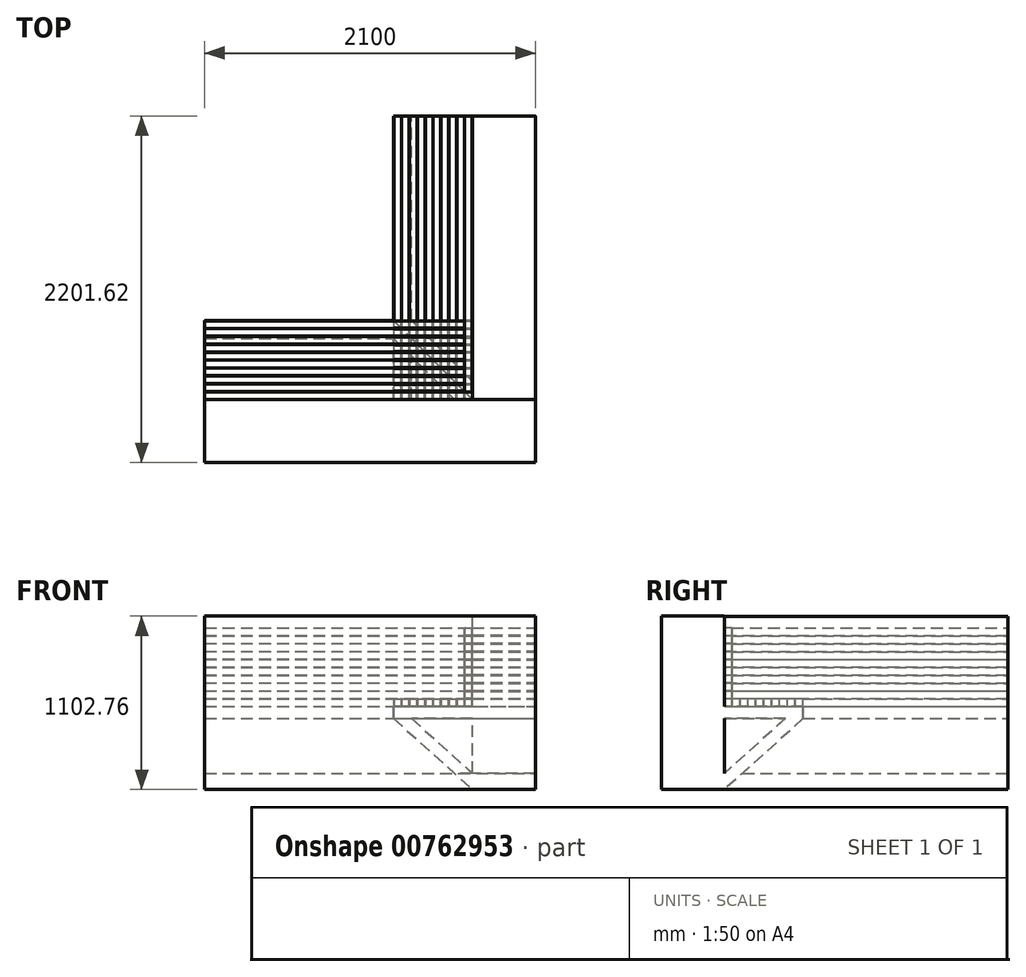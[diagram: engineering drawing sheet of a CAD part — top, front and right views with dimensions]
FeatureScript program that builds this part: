
annotation { "Feature Type Name" : "Feature", "Feature Type Description" : "" }
export const myFeature = defineFeature(function(context is Context, id is Id, definition is map)
    precondition{}
    {
        {
            var Q0;
            Q0=qCreatedBy(makeId("Front.planeOp"),FACE);
            var sketch = newSketch(context, id + "F0", { "sketchPlane" : qUnion([Q0])});
            skLineSegment(sketch, "E0", {"start": v(1, 650) * mm, "end": v(399, 650) * mm});
            skLineSegment(sketch, "E1", {"start": v(400, 649) * mm, "end": v(400, -449) * mm});
            skLineSegment(sketch, "E2", {"start": v(399, -450) * mm, "end": v(0, -450) * mm});
            skLineSegment(sketch, "E3", {"start": v(0, -450) * mm, "end": v(0, 0) * mm});
            skLineSegment(sketch, "E4", {"start": v(0, 0) * mm, "end": v(-500, 0) * mm});
            skLineSegment(sketch, "E5", {"start": v(-500, 0) * mm, "end": v(-500, 75.2) * mm});
            skLineSegment(sketch, "E6", {"start": v(-499, 76.2) * mm, "end": v(0, 76.2) * mm});
            skLineSegment(sketch, "E7", {"start": v(0, 76.2) * mm, "end": v(0, 649) * mm});
            skLineSegment(sketch, "E8", {"start": v(-500, 0) * mm, "end": v(0, -450) * mm});
            skLineSegment(sketch, "E9", {"start": v(-386.1, 0) * mm, "end": v(0, -347.48) * mm});
            skPoint(sketch, "E10.visualSharp", {"position": v(-500, 76.2) * mm});
            skArc(sketch, "E10.filletArc", {"start": v(-499, 76.2) * mm, "mid": v(-499.7, 75.9) * mm, "end": v(-500, 75.2) * mm});
            skPoint(sketch, "E11.visualSharp", {"position": v(0, 650) * mm});
            skArc(sketch, "E11.filletArc", {"start": v(1, 650) * mm, "mid": v(0.3, 649.7) * mm, "end": v(0, 649) * mm});
            skPoint(sketch, "E12.visualSharp", {"position": v(400, 650) * mm});
            skArc(sketch, "E12.filletArc", {"start": v(400, 649) * mm, "mid": v(399.7, 649.7) * mm, "end": v(399, 650) * mm});
            skPoint(sketch, "E13.visualSharp", {"position": v(400, -450) * mm});
            skArc(sketch, "E13.filletArc", {"start": v(399, -450) * mm, "mid": v(399.7, -449.7) * mm, "end": v(400, -449) * mm});
            skLineSegment(sketch, "E14.bottom", {"start": v(-4.84, 124.92) * mm, "end": v(-44.84, 124.92) * mm});
            skLineSegment(sketch, "E14.top", {"start": v(-4.84, 76.92) * mm, "end": v(-44.84, 76.92) * mm});
            skLineSegment(sketch, "E14.left", {"start": v(-0.84, 120.92) * mm, "end": v(-0.84, 80.92) * mm});
            skLineSegment(sketch, "E14.right", {"start": v(-48.84, 120.92) * mm, "end": v(-48.84, 80.92) * mm});
            skPoint(sketch, "E15.visualSharp", {"position": v(-48.84, 124.92) * mm});
            skArc(sketch, "E15.filletArc", {"start": v(-44.84, 124.92) * mm, "mid": v(-47.66, 123.75) * mm, "end": v(-48.84, 120.92) * mm});
            skPoint(sketch, "E16.visualSharp", {"position": v(-0.84, 124.92) * mm});
            skArc(sketch, "E16.filletArc", {"start": v(-0.84, 120.92) * mm, "mid": v(-2, 123.75) * mm, "end": v(-4.84, 124.92) * mm});
            skPoint(sketch, "E17.visualSharp", {"position": v(-48.84, 76.92) * mm});
            skArc(sketch, "E17.filletArc", {"start": v(-48.84, 80.92) * mm, "mid": v(-47.66, 78.1) * mm, "end": v(-44.84, 76.92) * mm});
            skPoint(sketch, "E18.visualSharp", {"position": v(-0.84, 76.92) * mm});
            skArc(sketch, "E18.filletArc", {"start": v(-4.84, 76.92) * mm, "mid": v(-2, 78.1) * mm, "end": v(-0.84, 80.92) * mm});
            skLineSegment(sketch, "E19.1.0.0", {"start": v(-50.84, 120.92) * mm, "end": v(-50.84, 80.92) * mm});
            skPoint(sketch, "E19.1.0.1", {"position": v(-50.84, 124.92) * mm});
            skArc(sketch, "E19.1.0.2", {"start": v(-50.84, 120.92) * mm, "mid": v(-52, 123.75) * mm, "end": v(-54.84, 124.92) * mm});
            skLineSegment(sketch, "E19.1.0.3", {"start": v(-54.84, 124.92) * mm, "end": v(-94.84, 124.92) * mm});
            skLineSegment(sketch, "E19.1.0.4", {"start": v(-98.84, 120.92) * mm, "end": v(-98.84, 80.92) * mm});
            skArc(sketch, "E19.1.0.5", {"start": v(-94.84, 124.92) * mm, "mid": v(-97.66, 123.75) * mm, "end": v(-98.84, 120.92) * mm});
            skArc(sketch, "E19.1.0.6", {"start": v(-98.84, 80.92) * mm, "mid": v(-97.66, 78.1) * mm, "end": v(-94.84, 76.92) * mm});
            skLineSegment(sketch, "E19.1.0.7", {"start": v(-54.84, 76.92) * mm, "end": v(-94.84, 76.92) * mm});
            skArc(sketch, "E19.1.0.8", {"start": v(-54.84, 76.92) * mm, "mid": v(-52, 78.1) * mm, "end": v(-50.84, 80.92) * mm});
            skLineSegment(sketch, "E19.2.0.0", {"start": v(-100.84, 120.92) * mm, "end": v(-100.84, 80.92) * mm});
            skPoint(sketch, "E19.2.0.1", {"position": v(-100.84, 124.92) * mm});
            skArc(sketch, "E19.2.0.2", {"start": v(-100.84, 120.92) * mm, "mid": v(-102, 123.75) * mm, "end": v(-104.84, 124.92) * mm});
            skLineSegment(sketch, "E19.2.0.3", {"start": v(-104.84, 124.92) * mm, "end": v(-144.84, 124.92) * mm});
            skLineSegment(sketch, "E19.2.0.4", {"start": v(-148.84, 120.92) * mm, "end": v(-148.84, 80.92) * mm});
            skArc(sketch, "E19.2.0.5", {"start": v(-144.84, 124.92) * mm, "mid": v(-147.66, 123.75) * mm, "end": v(-148.84, 120.92) * mm});
            skArc(sketch, "E19.2.0.6", {"start": v(-148.84, 80.92) * mm, "mid": v(-147.66, 78.1) * mm, "end": v(-144.84, 76.92) * mm});
            skLineSegment(sketch, "E19.2.0.7", {"start": v(-104.84, 76.92) * mm, "end": v(-144.84, 76.92) * mm});
            skArc(sketch, "E19.2.0.8", {"start": v(-104.84, 76.92) * mm, "mid": v(-102, 78.1) * mm, "end": v(-100.84, 80.92) * mm});
            skLineSegment(sketch, "E19.3.0.0", {"start": v(-150.84, 120.92) * mm, "end": v(-150.84, 80.92) * mm});
            skPoint(sketch, "E19.3.0.1", {"position": v(-150.84, 124.92) * mm});
            skArc(sketch, "E19.3.0.2", {"start": v(-150.84, 120.92) * mm, "mid": v(-152, 123.75) * mm, "end": v(-154.84, 124.92) * mm});
            skLineSegment(sketch, "E19.3.0.3", {"start": v(-154.84, 124.92) * mm, "end": v(-194.84, 124.92) * mm});
            skLineSegment(sketch, "E19.3.0.4", {"start": v(-198.84, 120.92) * mm, "end": v(-198.84, 80.92) * mm});
            skArc(sketch, "E19.3.0.5", {"start": v(-194.84, 124.92) * mm, "mid": v(-197.66, 123.75) * mm, "end": v(-198.84, 120.92) * mm});
            skArc(sketch, "E19.3.0.6", {"start": v(-198.84, 80.92) * mm, "mid": v(-197.66, 78.1) * mm, "end": v(-194.84, 76.92) * mm});
            skLineSegment(sketch, "E19.3.0.7", {"start": v(-154.84, 76.92) * mm, "end": v(-194.84, 76.92) * mm});
            skArc(sketch, "E19.3.0.8", {"start": v(-154.84, 76.92) * mm, "mid": v(-152, 78.1) * mm, "end": v(-150.84, 80.92) * mm});
            skLineSegment(sketch, "E19.4.0.0", {"start": v(-200.84, 120.92) * mm, "end": v(-200.84, 80.92) * mm});
            skPoint(sketch, "E19.4.0.1", {"position": v(-200.84, 124.92) * mm});
            skArc(sketch, "E19.4.0.2", {"start": v(-200.84, 120.92) * mm, "mid": v(-202, 123.75) * mm, "end": v(-204.84, 124.92) * mm});
            skLineSegment(sketch, "E19.4.0.3", {"start": v(-204.84, 124.92) * mm, "end": v(-244.84, 124.92) * mm});
            skLineSegment(sketch, "E19.4.0.4", {"start": v(-248.84, 120.92) * mm, "end": v(-248.84, 80.92) * mm});
            skArc(sketch, "E19.4.0.5", {"start": v(-244.84, 124.92) * mm, "mid": v(-247.66, 123.75) * mm, "end": v(-248.84, 120.92) * mm});
            skArc(sketch, "E19.4.0.6", {"start": v(-248.84, 80.92) * mm, "mid": v(-247.66, 78.1) * mm, "end": v(-244.84, 76.92) * mm});
            skLineSegment(sketch, "E19.4.0.7", {"start": v(-204.84, 76.92) * mm, "end": v(-244.84, 76.92) * mm});
            skArc(sketch, "E19.4.0.8", {"start": v(-204.84, 76.92) * mm, "mid": v(-202, 78.1) * mm, "end": v(-200.84, 80.92) * mm});
            skLineSegment(sketch, "E19.5.0.0", {"start": v(-250.84, 120.92) * mm, "end": v(-250.84, 80.92) * mm});
            skPoint(sketch, "E19.5.0.1", {"position": v(-250.84, 124.92) * mm});
            skArc(sketch, "E19.5.0.2", {"start": v(-250.84, 120.92) * mm, "mid": v(-252, 123.75) * mm, "end": v(-254.84, 124.92) * mm});
            skLineSegment(sketch, "E19.5.0.3", {"start": v(-254.84, 124.92) * mm, "end": v(-294.84, 124.92) * mm});
            skLineSegment(sketch, "E19.5.0.4", {"start": v(-298.84, 120.92) * mm, "end": v(-298.84, 80.92) * mm});
            skArc(sketch, "E19.5.0.5", {"start": v(-294.84, 124.92) * mm, "mid": v(-297.66, 123.75) * mm, "end": v(-298.84, 120.92) * mm});
            skArc(sketch, "E19.5.0.6", {"start": v(-298.84, 80.92) * mm, "mid": v(-297.66, 78.1) * mm, "end": v(-294.84, 76.92) * mm});
            skLineSegment(sketch, "E19.5.0.7", {"start": v(-254.84, 76.92) * mm, "end": v(-294.84, 76.92) * mm});
            skArc(sketch, "E19.5.0.8", {"start": v(-254.84, 76.92) * mm, "mid": v(-252, 78.1) * mm, "end": v(-250.84, 80.92) * mm});
            skLineSegment(sketch, "E19.6.0.0", {"start": v(-300.84, 120.92) * mm, "end": v(-300.84, 80.92) * mm});
            skPoint(sketch, "E19.6.0.1", {"position": v(-300.84, 124.92) * mm});
            skArc(sketch, "E19.6.0.2", {"start": v(-300.84, 120.92) * mm, "mid": v(-302, 123.75) * mm, "end": v(-304.84, 124.92) * mm});
            skLineSegment(sketch, "E19.6.0.3", {"start": v(-304.84, 124.92) * mm, "end": v(-344.84, 124.92) * mm});
            skLineSegment(sketch, "E19.6.0.4", {"start": v(-348.84, 120.92) * mm, "end": v(-348.84, 80.92) * mm});
            skArc(sketch, "E19.6.0.5", {"start": v(-344.84, 124.92) * mm, "mid": v(-347.66, 123.75) * mm, "end": v(-348.84, 120.92) * mm});
            skArc(sketch, "E19.6.0.6", {"start": v(-348.84, 80.92) * mm, "mid": v(-347.66, 78.1) * mm, "end": v(-344.84, 76.92) * mm});
            skLineSegment(sketch, "E19.6.0.7", {"start": v(-304.84, 76.92) * mm, "end": v(-344.84, 76.92) * mm});
            skArc(sketch, "E19.6.0.8", {"start": v(-304.84, 76.92) * mm, "mid": v(-302, 78.1) * mm, "end": v(-300.84, 80.92) * mm});
            skLineSegment(sketch, "E19.7.0.0", {"start": v(-350.84, 120.92) * mm, "end": v(-350.84, 80.92) * mm});
            skPoint(sketch, "E19.7.0.1", {"position": v(-350.84, 124.92) * mm});
            skArc(sketch, "E19.7.0.2", {"start": v(-350.84, 120.92) * mm, "mid": v(-352, 123.75) * mm, "end": v(-354.84, 124.92) * mm});
            skLineSegment(sketch, "E19.7.0.3", {"start": v(-354.84, 124.92) * mm, "end": v(-394.84, 124.92) * mm});
            skLineSegment(sketch, "E19.7.0.4", {"start": v(-398.84, 120.92) * mm, "end": v(-398.84, 80.92) * mm});
            skArc(sketch, "E19.7.0.5", {"start": v(-394.84, 124.92) * mm, "mid": v(-397.66, 123.75) * mm, "end": v(-398.84, 120.92) * mm});
            skArc(sketch, "E19.7.0.6", {"start": v(-398.84, 80.92) * mm, "mid": v(-397.66, 78.1) * mm, "end": v(-394.84, 76.92) * mm});
            skLineSegment(sketch, "E19.7.0.7", {"start": v(-354.84, 76.92) * mm, "end": v(-394.84, 76.92) * mm});
            skArc(sketch, "E19.7.0.8", {"start": v(-354.84, 76.92) * mm, "mid": v(-352, 78.1) * mm, "end": v(-350.84, 80.92) * mm});
            skLineSegment(sketch, "E19.8.0.0", {"start": v(-400.84, 120.92) * mm, "end": v(-400.84, 80.92) * mm});
            skPoint(sketch, "E19.8.0.1", {"position": v(-400.84, 124.92) * mm});
            skArc(sketch, "E19.8.0.2", {"start": v(-400.84, 120.92) * mm, "mid": v(-402, 123.75) * mm, "end": v(-404.84, 124.92) * mm});
            skLineSegment(sketch, "E19.8.0.3", {"start": v(-404.84, 124.92) * mm, "end": v(-444.84, 124.92) * mm});
            skLineSegment(sketch, "E19.8.0.4", {"start": v(-448.84, 120.92) * mm, "end": v(-448.84, 80.92) * mm});
            skArc(sketch, "E19.8.0.5", {"start": v(-444.84, 124.92) * mm, "mid": v(-447.66, 123.75) * mm, "end": v(-448.84, 120.92) * mm});
            skArc(sketch, "E19.8.0.6", {"start": v(-448.84, 80.92) * mm, "mid": v(-447.66, 78.1) * mm, "end": v(-444.84, 76.92) * mm});
            skLineSegment(sketch, "E19.8.0.7", {"start": v(-404.84, 76.92) * mm, "end": v(-444.84, 76.92) * mm});
            skArc(sketch, "E19.8.0.8", {"start": v(-404.84, 76.92) * mm, "mid": v(-402, 78.1) * mm, "end": v(-400.84, 80.92) * mm});
            skLineSegment(sketch, "E19.9.0.0", {"start": v(-450.84, 120.92) * mm, "end": v(-450.84, 80.92) * mm});
            skPoint(sketch, "E19.9.0.1", {"position": v(-450.84, 124.92) * mm});
            skArc(sketch, "E19.9.0.2", {"start": v(-450.84, 120.92) * mm, "mid": v(-452, 123.75) * mm, "end": v(-454.84, 124.92) * mm});
            skLineSegment(sketch, "E19.9.0.3", {"start": v(-454.84, 124.92) * mm, "end": v(-494.84, 124.92) * mm});
            skLineSegment(sketch, "E19.9.0.4", {"start": v(-498.84, 120.92) * mm, "end": v(-498.84, 80.92) * mm});
            skArc(sketch, "E19.9.0.5", {"start": v(-494.84, 124.92) * mm, "mid": v(-497.66, 123.75) * mm, "end": v(-498.84, 120.92) * mm});
            skArc(sketch, "E19.9.0.6", {"start": v(-498.84, 80.92) * mm, "mid": v(-497.66, 78.1) * mm, "end": v(-494.84, 76.92) * mm});
            skLineSegment(sketch, "E19.9.0.7", {"start": v(-454.84, 76.92) * mm, "end": v(-494.84, 76.92) * mm});
            skArc(sketch, "E19.9.0.8", {"start": v(-454.84, 76.92) * mm, "mid": v(-452, 78.1) * mm, "end": v(-450.84, 80.92) * mm});
            skLineSegment(sketch, "E19.direction1", {"start": v(-0.84, 80.92) * mm, "end": v(-50.84, 80.92) * mm, "construction": true});
            skLineSegment(sketch, "E20.0.1.0", {"start": v(-4.84, 174.92) * mm, "end": v(-44.84, 174.92) * mm});
            skArc(sketch, "E20.0.1.1", {"start": v(-44.84, 174.92) * mm, "mid": v(-47.66, 173.75) * mm, "end": v(-48.84, 170.92) * mm});
            skArc(sketch, "E20.0.1.2", {"start": v(-0.84, 170.92) * mm, "mid": v(-2, 173.75) * mm, "end": v(-4.84, 174.92) * mm});
            skLineSegment(sketch, "E20.0.1.3", {"start": v(-0.84, 170.92) * mm, "end": v(-0.84, 130.92) * mm});
            skArc(sketch, "E20.0.1.4", {"start": v(-4.84, 126.92) * mm, "mid": v(-2, 128.1) * mm, "end": v(-0.84, 130.92) * mm});
            skLineSegment(sketch, "E20.0.1.5", {"start": v(-4.84, 126.92) * mm, "end": v(-44.84, 126.92) * mm});
            skArc(sketch, "E20.0.1.6", {"start": v(-48.84, 130.92) * mm, "mid": v(-47.66, 128.1) * mm, "end": v(-44.84, 126.92) * mm});
            skLineSegment(sketch, "E20.0.1.7", {"start": v(-48.84, 170.92) * mm, "end": v(-48.84, 130.92) * mm});
            skLineSegment(sketch, "E20.0.2.0", {"start": v(-4.84, 224.92) * mm, "end": v(-44.84, 224.92) * mm});
            skArc(sketch, "E20.0.2.1", {"start": v(-44.84, 224.92) * mm, "mid": v(-47.66, 223.75) * mm, "end": v(-48.84, 220.92) * mm});
            skArc(sketch, "E20.0.2.2", {"start": v(-0.84, 220.92) * mm, "mid": v(-2, 223.75) * mm, "end": v(-4.84, 224.92) * mm});
            skLineSegment(sketch, "E20.0.2.3", {"start": v(-0.84, 220.92) * mm, "end": v(-0.84, 180.92) * mm});
            skArc(sketch, "E20.0.2.4", {"start": v(-4.84, 176.92) * mm, "mid": v(-2, 178.1) * mm, "end": v(-0.84, 180.92) * mm});
            skLineSegment(sketch, "E20.0.2.5", {"start": v(-4.84, 176.92) * mm, "end": v(-44.84, 176.92) * mm});
            skArc(sketch, "E20.0.2.6", {"start": v(-48.84, 180.92) * mm, "mid": v(-47.66, 178.1) * mm, "end": v(-44.84, 176.92) * mm});
            skLineSegment(sketch, "E20.0.2.7", {"start": v(-48.84, 220.92) * mm, "end": v(-48.84, 180.92) * mm});
            skLineSegment(sketch, "E20.0.3.0", {"start": v(-4.84, 274.92) * mm, "end": v(-44.84, 274.92) * mm});
            skArc(sketch, "E20.0.3.1", {"start": v(-44.84, 274.92) * mm, "mid": v(-47.66, 273.75) * mm, "end": v(-48.84, 270.92) * mm});
            skArc(sketch, "E20.0.3.2", {"start": v(-0.84, 270.92) * mm, "mid": v(-2, 273.75) * mm, "end": v(-4.84, 274.92) * mm});
            skLineSegment(sketch, "E20.0.3.3", {"start": v(-0.84, 270.92) * mm, "end": v(-0.84, 230.92) * mm});
            skArc(sketch, "E20.0.3.4", {"start": v(-4.84, 226.92) * mm, "mid": v(-2, 228.1) * mm, "end": v(-0.84, 230.92) * mm});
            skLineSegment(sketch, "E20.0.3.5", {"start": v(-4.84, 226.92) * mm, "end": v(-44.84, 226.92) * mm});
            skArc(sketch, "E20.0.3.6", {"start": v(-48.84, 230.92) * mm, "mid": v(-47.66, 228.1) * mm, "end": v(-44.84, 226.92) * mm});
            skLineSegment(sketch, "E20.0.3.7", {"start": v(-48.84, 270.92) * mm, "end": v(-48.84, 230.92) * mm});
            skLineSegment(sketch, "E20.0.4.0", {"start": v(-4.84, 324.92) * mm, "end": v(-44.84, 324.92) * mm});
            skArc(sketch, "E20.0.4.1", {"start": v(-44.84, 324.92) * mm, "mid": v(-47.66, 323.75) * mm, "end": v(-48.84, 320.92) * mm});
            skArc(sketch, "E20.0.4.2", {"start": v(-0.84, 320.92) * mm, "mid": v(-2, 323.75) * mm, "end": v(-4.84, 324.92) * mm});
            skLineSegment(sketch, "E20.0.4.3", {"start": v(-0.84, 320.92) * mm, "end": v(-0.84, 280.92) * mm});
            skArc(sketch, "E20.0.4.4", {"start": v(-4.84, 276.92) * mm, "mid": v(-2, 278.1) * mm, "end": v(-0.84, 280.92) * mm});
            skLineSegment(sketch, "E20.0.4.5", {"start": v(-4.84, 276.92) * mm, "end": v(-44.84, 276.92) * mm});
            skArc(sketch, "E20.0.4.6", {"start": v(-48.84, 280.92) * mm, "mid": v(-47.66, 278.1) * mm, "end": v(-44.84, 276.92) * mm});
            skLineSegment(sketch, "E20.0.4.7", {"start": v(-48.84, 320.92) * mm, "end": v(-48.84, 280.92) * mm});
            skLineSegment(sketch, "E20.0.5.0", {"start": v(-4.84, 374.92) * mm, "end": v(-44.84, 374.92) * mm});
            skArc(sketch, "E20.0.5.1", {"start": v(-44.84, 374.92) * mm, "mid": v(-47.66, 373.75) * mm, "end": v(-48.84, 370.92) * mm});
            skArc(sketch, "E20.0.5.2", {"start": v(-0.84, 370.92) * mm, "mid": v(-2, 373.75) * mm, "end": v(-4.84, 374.92) * mm});
            skLineSegment(sketch, "E20.0.5.3", {"start": v(-0.84, 370.92) * mm, "end": v(-0.84, 330.92) * mm});
            skArc(sketch, "E20.0.5.4", {"start": v(-4.84, 326.92) * mm, "mid": v(-2, 328.1) * mm, "end": v(-0.84, 330.92) * mm});
            skLineSegment(sketch, "E20.0.5.5", {"start": v(-4.84, 326.92) * mm, "end": v(-44.84, 326.92) * mm});
            skArc(sketch, "E20.0.5.6", {"start": v(-48.84, 330.92) * mm, "mid": v(-47.66, 328.1) * mm, "end": v(-44.84, 326.92) * mm});
            skLineSegment(sketch, "E20.0.5.7", {"start": v(-48.84, 370.92) * mm, "end": v(-48.84, 330.92) * mm});
            skLineSegment(sketch, "E20.0.6.0", {"start": v(-4.84, 424.92) * mm, "end": v(-44.84, 424.92) * mm});
            skArc(sketch, "E20.0.6.1", {"start": v(-44.84, 424.92) * mm, "mid": v(-47.66, 423.75) * mm, "end": v(-48.84, 420.92) * mm});
            skArc(sketch, "E20.0.6.2", {"start": v(-0.84, 420.92) * mm, "mid": v(-2, 423.75) * mm, "end": v(-4.84, 424.92) * mm});
            skLineSegment(sketch, "E20.0.6.3", {"start": v(-0.84, 420.92) * mm, "end": v(-0.84, 380.92) * mm});
            skArc(sketch, "E20.0.6.4", {"start": v(-4.84, 376.92) * mm, "mid": v(-2, 378.1) * mm, "end": v(-0.84, 380.92) * mm});
            skLineSegment(sketch, "E20.0.6.5", {"start": v(-4.84, 376.92) * mm, "end": v(-44.84, 376.92) * mm});
            skArc(sketch, "E20.0.6.6", {"start": v(-48.84, 380.92) * mm, "mid": v(-47.66, 378.1) * mm, "end": v(-44.84, 376.92) * mm});
            skLineSegment(sketch, "E20.0.6.7", {"start": v(-48.84, 420.92) * mm, "end": v(-48.84, 380.92) * mm});
            skLineSegment(sketch, "E20.0.7.0", {"start": v(-4.84, 474.92) * mm, "end": v(-44.84, 474.92) * mm});
            skArc(sketch, "E20.0.7.1", {"start": v(-44.84, 474.92) * mm, "mid": v(-47.66, 473.75) * mm, "end": v(-48.84, 470.92) * mm});
            skArc(sketch, "E20.0.7.2", {"start": v(-0.84, 470.92) * mm, "mid": v(-2, 473.75) * mm, "end": v(-4.84, 474.92) * mm});
            skLineSegment(sketch, "E20.0.7.3", {"start": v(-0.84, 470.92) * mm, "end": v(-0.84, 430.92) * mm});
            skArc(sketch, "E20.0.7.4", {"start": v(-4.84, 426.92) * mm, "mid": v(-2, 428.1) * mm, "end": v(-0.84, 430.92) * mm});
            skLineSegment(sketch, "E20.0.7.5", {"start": v(-4.84, 426.92) * mm, "end": v(-44.84, 426.92) * mm});
            skArc(sketch, "E20.0.7.6", {"start": v(-48.84, 430.92) * mm, "mid": v(-47.66, 428.1) * mm, "end": v(-44.84, 426.92) * mm});
            skLineSegment(sketch, "E20.0.7.7", {"start": v(-48.84, 470.92) * mm, "end": v(-48.84, 430.92) * mm});
            skLineSegment(sketch, "E20.0.8.0", {"start": v(-4.84, 524.92) * mm, "end": v(-44.84, 524.92) * mm});
            skArc(sketch, "E20.0.8.1", {"start": v(-44.84, 524.92) * mm, "mid": v(-47.66, 523.75) * mm, "end": v(-48.84, 520.92) * mm});
            skArc(sketch, "E20.0.8.2", {"start": v(-0.84, 520.92) * mm, "mid": v(-2, 523.75) * mm, "end": v(-4.84, 524.92) * mm});
            skLineSegment(sketch, "E20.0.8.3", {"start": v(-0.84, 520.92) * mm, "end": v(-0.84, 480.92) * mm});
            skArc(sketch, "E20.0.8.4", {"start": v(-4.84, 476.92) * mm, "mid": v(-2, 478.1) * mm, "end": v(-0.84, 480.92) * mm});
            skLineSegment(sketch, "E20.0.8.5", {"start": v(-4.84, 476.92) * mm, "end": v(-44.84, 476.92) * mm});
            skArc(sketch, "E20.0.8.6", {"start": v(-48.84, 480.92) * mm, "mid": v(-47.66, 478.1) * mm, "end": v(-44.84, 476.92) * mm});
            skLineSegment(sketch, "E20.0.8.7", {"start": v(-48.84, 520.92) * mm, "end": v(-48.84, 480.92) * mm});
            skLineSegment(sketch, "E20.0.9.0", {"start": v(-4.84, 574.92) * mm, "end": v(-44.84, 574.92) * mm});
            skArc(sketch, "E20.0.9.1", {"start": v(-44.84, 574.92) * mm, "mid": v(-47.66, 573.75) * mm, "end": v(-48.84, 570.92) * mm});
            skArc(sketch, "E20.0.9.2", {"start": v(-0.84, 570.92) * mm, "mid": v(-2, 573.75) * mm, "end": v(-4.84, 574.92) * mm});
            skLineSegment(sketch, "E20.0.9.3", {"start": v(-0.84, 570.92) * mm, "end": v(-0.84, 530.92) * mm});
            skArc(sketch, "E20.0.9.4", {"start": v(-4.84, 526.92) * mm, "mid": v(-2, 528.1) * mm, "end": v(-0.84, 530.92) * mm});
            skLineSegment(sketch, "E20.0.9.5", {"start": v(-4.84, 526.92) * mm, "end": v(-44.84, 526.92) * mm});
            skArc(sketch, "E20.0.9.6", {"start": v(-48.84, 530.92) * mm, "mid": v(-47.66, 528.1) * mm, "end": v(-44.84, 526.92) * mm});
            skLineSegment(sketch, "E20.0.9.7", {"start": v(-48.84, 570.92) * mm, "end": v(-48.84, 530.92) * mm});
            skLineSegment(sketch, "E20.direction1", {"start": v(-44.84, 124.92) * mm, "end": v(-19.84, 124.92) * mm, "construction": true});
            skLineSegment(sketch, "E20.direction2", {"start": v(-44.84, 124.92) * mm, "end": v(-44.84, 174.92) * mm, "construction": true});
            skSolve(sketch);
        }
        {
            var Q0;
            {var subQ0=sQuery(id+"F0.wireOp",EDGE,"E8");Q0=makeQuery(id+"F0.imprint","IMPRINT",FACE,{"disambiguationData":[TD([[makeQuery(id+"F0.imprint","IMPRINT",EDGE,{"derivedFrom":subQ0}),1.0]])]});}
            var Q1;
            Q1=makeQuery(id+"F0.imprint","IMPRINT",FACE,{"disambiguationData":[TD([[makeQuery(id+"F0.imprint","IMPRINT",EDGE,{"derivedFrom":sQuery(id+"F0.wireOp",EDGE,"E0")}),-1.0]])]});
            extrude(context, id + "F1", {"entities" : qUnion([Q0, Q1]), "depth" : 1800 * mm, "offsetDistance" : 25 * mm});
        }
        {
            var Q0;
            Q0=makeQuery(id+"F1.opExtrude","SWEPT_FACE",FACE,{"disambiguationData":[OSD([sQuery(id+"F0.wireOp",EDGE,"E1")])]});
            cPlane(context, id + "F2", {"entities" : qUnion([Q0]), "cplaneType" : CPlaneType.OFFSET, "offset" : 0 * mm, "width" : 150 * mm, "height" : 150 * mm});
        }
        {
            var Q0;
            Q0=makeQuery(id+"F0.imprint","IMPRINT",FACE,{"disambiguationData":[TD([[makeQuery(id+"F0.imprint","IMPRINT",EDGE,{"derivedFrom":sQuery(id+"F0.wireOp",EDGE,"E19.9.0.0")}),-1.0]])]});
            var Q1;
            Q1=makeQuery(id+"F0.imprint","IMPRINT",FACE,{"disambiguationData":[TD([[makeQuery(id+"F0.imprint","IMPRINT",EDGE,{"derivedFrom":sQuery(id+"F0.wireOp",EDGE,"E19.8.0.0")}),-1.0]])]});
            var Q2;
            Q2=makeQuery(id+"F0.imprint","IMPRINT",FACE,{"disambiguationData":[TD([[makeQuery(id+"F0.imprint","IMPRINT",EDGE,{"derivedFrom":sQuery(id+"F0.wireOp",EDGE,"E19.7.0.0")}),-1.0]])]});
            var Q3;
            Q3=makeQuery(id+"F0.imprint","IMPRINT",FACE,{"disambiguationData":[TD([[makeQuery(id+"F0.imprint","IMPRINT",EDGE,{"derivedFrom":sQuery(id+"F0.wireOp",EDGE,"E19.6.0.0")}),-1.0]])]});
            var Q4;
            Q4=makeQuery(id+"F0.imprint","IMPRINT",FACE,{"disambiguationData":[TD([[makeQuery(id+"F0.imprint","IMPRINT",EDGE,{"derivedFrom":sQuery(id+"F0.wireOp",EDGE,"E19.5.0.0")}),-1.0]])]});
            var Q5;
            Q5=makeQuery(id+"F0.imprint","IMPRINT",FACE,{"disambiguationData":[TD([[makeQuery(id+"F0.imprint","IMPRINT",EDGE,{"derivedFrom":sQuery(id+"F0.wireOp",EDGE,"E19.4.0.0")}),-1.0]])]});
            var Q6;
            Q6=makeQuery(id+"F0.imprint","IMPRINT",FACE,{"disambiguationData":[TD([[makeQuery(id+"F0.imprint","IMPRINT",EDGE,{"derivedFrom":sQuery(id+"F0.wireOp",EDGE,"E19.3.0.0")}),-1.0]])]});
            var Q7;
            Q7=makeQuery(id+"F0.imprint","IMPRINT",FACE,{"disambiguationData":[TD([[makeQuery(id+"F0.imprint","IMPRINT",EDGE,{"derivedFrom":sQuery(id+"F0.wireOp",EDGE,"E19.2.0.0")}),-1.0]])]});
            var Q8;
            Q8=makeQuery(id+"F0.imprint","IMPRINT",FACE,{"disambiguationData":[TD([[makeQuery(id+"F0.imprint","IMPRINT",EDGE,{"derivedFrom":sQuery(id+"F0.wireOp",EDGE,"E19.1.0.0")}),-1.0]])]});
            var Q9;
            Q9=makeQuery(id+"F0.imprint","IMPRINT",FACE,{"disambiguationData":[TD([[makeQuery(id+"F0.imprint","IMPRINT",EDGE,{"derivedFrom":sQuery(id+"F0.wireOp",EDGE,"E14.bottom")}),1.0]])]});
            extrude(context, id + "F3", {"entities" : qUnion([Q0, Q1, Q2, Q3, Q4, Q5, Q6, Q7, Q8, Q9]), "depth" : 1800 * mm, "offsetDistance" : 25 * mm});
        }
        {
            var Q0;
            Q0=makeQuery(id+"F0.imprint","IMPRINT",FACE,{"disambiguationData":[TD([[makeQuery(id+"F0.imprint","IMPRINT",EDGE,{"derivedFrom":sQuery(id+"F0.wireOp",EDGE,"E20.0.2.0")}),1.0]])]});
            var Q1;
            Q1=makeQuery(id+"F0.imprint","IMPRINT",FACE,{"disambiguationData":[TD([[makeQuery(id+"F0.imprint","IMPRINT",EDGE,{"derivedFrom":sQuery(id+"F0.wireOp",EDGE,"E20.0.3.0")}),1.0]])]});
            var Q2;
            Q2=makeQuery(id+"F0.imprint","IMPRINT",FACE,{"disambiguationData":[TD([[makeQuery(id+"F0.imprint","IMPRINT",EDGE,{"derivedFrom":sQuery(id+"F0.wireOp",EDGE,"E20.0.4.0")}),1.0]])]});
            var Q3;
            Q3=makeQuery(id+"F0.imprint","IMPRINT",FACE,{"disambiguationData":[TD([[makeQuery(id+"F0.imprint","IMPRINT",EDGE,{"derivedFrom":sQuery(id+"F0.wireOp",EDGE,"E20.0.5.0")}),1.0]])]});
            var Q4;
            Q4=makeQuery(id+"F0.imprint","IMPRINT",FACE,{"disambiguationData":[TD([[makeQuery(id+"F0.imprint","IMPRINT",EDGE,{"derivedFrom":sQuery(id+"F0.wireOp",EDGE,"E20.0.6.0")}),1.0]])]});
            var Q5;
            Q5=makeQuery(id+"F0.imprint","IMPRINT",FACE,{"disambiguationData":[TD([[makeQuery(id+"F0.imprint","IMPRINT",EDGE,{"derivedFrom":sQuery(id+"F0.wireOp",EDGE,"E20.0.7.0")}),1.0]])]});
            var Q6;
            Q6=makeQuery(id+"F0.imprint","IMPRINT",FACE,{"disambiguationData":[TD([[makeQuery(id+"F0.imprint","IMPRINT",EDGE,{"derivedFrom":sQuery(id+"F0.wireOp",EDGE,"E20.0.8.0")}),1.0]])]});
            var Q7;
            Q7=makeQuery(id+"F0.imprint","IMPRINT",FACE,{"disambiguationData":[TD([[makeQuery(id+"F0.imprint","IMPRINT",EDGE,{"derivedFrom":sQuery(id+"F0.wireOp",EDGE,"E20.0.9.0")}),1.0]])]});
            var Q8;
            Q8=makeQuery(id+"F0.imprint","IMPRINT",FACE,{"disambiguationData":[TD([[makeQuery(id+"F0.imprint","IMPRINT",EDGE,{"derivedFrom":sQuery(id+"F0.wireOp",EDGE,"E20.0.1.0")}),1.0]])]});
            extrude(context, id + "F4", {"entities" : qUnion([Q0, Q1, Q2, Q3, Q4, Q5, Q6, Q7, Q8]), "depth" : 1800 * mm, "offsetDistance" : 25 * mm});
        }
        {
            var Q0;
            Q0=qCreatedBy(id+"F2.planeOp",FACE);
            var sketch = newSketch(context, id + "F5", { "sketchPlane" : qUnion([Q0])});
            skArc(sketch, "E21.MirrorCS", {"start": v(-1750.66, 121.34) * mm, "mid": v(-1749.49, 124.18) * mm, "end": v(-1746.65, 125.35) * mm});
            skArc(sketch, "E22.MirrorCS", {"start": v(-1756.68, 125.35) * mm, "mid": v(-1753.84, 124.18) * mm, "end": v(-1752.67, 121.34) * mm});
            skLineSegment(sketch, "E23.MirrorCS", {"start": v(-1752.67, 171.47) * mm, "end": v(-1752.67, 131.36) * mm});
            skLineSegment(sketch, "E24.MirrorCS", {"start": v(-1756.68, 125.35) * mm, "end": v(-1781.74, 125.35) * mm, "construction": true});
            skArc(sketch, "E25.MirrorCS", {"start": v(-1752.67, 131.36) * mm, "mid": v(-1753.84, 128.53) * mm, "end": v(-1756.68, 127.35) * mm});
            skLineSegment(sketch, "E26.MirrorCS", {"start": v(-1756.68, 125.35) * mm, "end": v(-1756.68, 175.48) * mm, "construction": true});
            skArc(sketch, "E27.MirrorCS", {"start": v(-1752.67, 181.5) * mm, "mid": v(-1753.84, 178.65) * mm, "end": v(-1756.68, 177.48) * mm});
            skArc(sketch, "E28.MirrorCS", {"start": v(-1756.68, 175.48) * mm, "mid": v(-1753.84, 174.3) * mm, "end": v(-1752.67, 171.47) * mm});
            skLineSegment(sketch, "E29.MirrorCS", {"start": v(-1750.66, 121.34) * mm, "end": v(-1750.66, 81.24) * mm});
            skArc(sketch, "E30.MirrorCS", {"start": v(-1756.68, 426.1) * mm, "mid": v(-1753.84, 424.93) * mm, "end": v(-1752.67, 422.1) * mm});
            skArc(sketch, "E31.MirrorCS", {"start": v(-1796.78, 478.23) * mm, "mid": v(-1799.61, 479.4) * mm, "end": v(-1800.79, 482.24) * mm});
            skLineSegment(sketch, "E32.MirrorCS", {"start": v(-1796.78, 478.23) * mm, "end": v(-1756.68, 478.23) * mm});
            skLineSegment(sketch, "E33.MirrorCS", {"start": v(-1796.78, 175.48) * mm, "end": v(-1756.68, 175.48) * mm});
            skLineSegment(sketch, "E34.MirrorCS", {"start": v(-1796.78, 476.23) * mm, "end": v(-1756.68, 476.23) * mm});
            skArc(sketch, "E35.MirrorCS", {"start": v(-1800.79, 472.22) * mm, "mid": v(-1799.61, 475.05) * mm, "end": v(-1796.78, 476.23) * mm});
            skArc(sketch, "E36.MirrorCS", {"start": v(-1796.78, 127.35) * mm, "mid": v(-1799.61, 128.53) * mm, "end": v(-1800.79, 131.36) * mm});
            skArc(sketch, "E37.MirrorCS", {"start": v(-1752.67, 432.12) * mm, "mid": v(-1753.84, 429.28) * mm, "end": v(-1756.68, 428.1) * mm});
            skLineSegment(sketch, "E38.MirrorCS", {"start": v(-1550.16, 121.34) * mm, "end": v(-1550.16, 81.24) * mm});
            skLineSegment(sketch, "E39.MirrorCS", {"start": v(-1349.66, 121.34) * mm, "end": v(-1349.66, 81.24) * mm});
            skLineSegment(sketch, "E40.MirrorCS", {"start": v(-1752.67, 472.22) * mm, "end": v(-1752.67, 432.12) * mm});
            skArc(sketch, "E41.MirrorCS", {"start": v(-1349.66, 121.34) * mm, "mid": v(-1348.48, 124.18) * mm, "end": v(-1345.65, 125.35) * mm});
            skArc(sketch, "E42.MirrorCS", {"start": v(-1449.9, 121.34) * mm, "mid": v(-1448.73, 124.18) * mm, "end": v(-1445.9, 125.35) * mm});
            skArc(sketch, "E43.MirrorCS", {"start": v(-1550.16, 121.34) * mm, "mid": v(-1548.98, 124.18) * mm, "end": v(-1546.15, 125.35) * mm});
            skArc(sketch, "E44.MirrorCS", {"start": v(-1650.41, 121.34) * mm, "mid": v(-1649.24, 124.18) * mm, "end": v(-1646.4, 125.35) * mm});
            skLineSegment(sketch, "E45.MirrorCS", {"start": v(-1746.65, 125.35) * mm, "end": v(-1706.55, 125.35) * mm});
            skLineSegment(sketch, "E46.MirrorCS", {"start": v(-1702.54, 121.34) * mm, "end": v(-1702.54, 81.24) * mm});
            skLineSegment(sketch, "E47.MirrorCS", {"start": v(-1502.04, 121.34) * mm, "end": v(-1502.04, 81.24) * mm});
            skArc(sketch, "E48.MirrorCS", {"start": v(-1800.79, 321.84) * mm, "mid": v(-1799.61, 324.68) * mm, "end": v(-1796.78, 325.85) * mm});
            skArc(sketch, "E49.MirrorCS", {"start": v(-1706.55, 125.35) * mm, "mid": v(-1703.71, 124.18) * mm, "end": v(-1702.54, 121.34) * mm});
            skArc(sketch, "E50.MirrorCS", {"start": v(-1405.8, 125.35) * mm, "mid": v(-1402.96, 124.18) * mm, "end": v(-1401.79, 121.34) * mm});
            skArc(sketch, "E51.MirrorCS", {"start": v(-1506.05, 125.35) * mm, "mid": v(-1503.21, 124.18) * mm, "end": v(-1502.04, 121.34) * mm});
            skArc(sketch, "E52.MirrorCS", {"start": v(-1606.3, 125.35) * mm, "mid": v(-1603.46, 124.18) * mm, "end": v(-1602.29, 121.34) * mm});
            skArc(sketch, "E53.MirrorCS", {"start": v(-1702.54, 81.24) * mm, "mid": v(-1703.71, 78.4) * mm, "end": v(-1706.55, 77.23) * mm});
            skArc(sketch, "E54.MirrorCS", {"start": v(-1502.04, 81.24) * mm, "mid": v(-1503.21, 78.4) * mm, "end": v(-1506.05, 77.23) * mm});
            skArc(sketch, "E55.MirrorCS", {"start": v(-1602.29, 81.24) * mm, "mid": v(-1603.46, 78.4) * mm, "end": v(-1606.3, 77.23) * mm});
            skArc(sketch, "E56.MirrorCS", {"start": v(-1796.78, 177.48) * mm, "mid": v(-1799.61, 178.65) * mm, "end": v(-1800.79, 181.5) * mm});
            skArc(sketch, "E57.MirrorCS", {"start": v(-1752.67, 482.24) * mm, "mid": v(-1753.84, 479.4) * mm, "end": v(-1756.68, 478.23) * mm});
            skArc(sketch, "E58.MirrorCS", {"start": v(-1752.67, 382) * mm, "mid": v(-1753.84, 379.16) * mm, "end": v(-1756.68, 377.98) * mm});
            skLineSegment(sketch, "E59.MirrorCS", {"start": v(-1796.78, 177.48) * mm, "end": v(-1756.68, 177.48) * mm});
            skArc(sketch, "E60.MirrorCS", {"start": v(-1756.68, 476.23) * mm, "mid": v(-1753.84, 475.05) * mm, "end": v(-1752.67, 472.22) * mm});
            skArc(sketch, "E61.MirrorCS", {"start": v(-1800.79, 171.47) * mm, "mid": v(-1799.61, 174.3) * mm, "end": v(-1796.78, 175.48) * mm});
            skLineSegment(sketch, "E62.MirrorCS", {"start": v(-1351.66, 121.34) * mm, "end": v(-1351.66, 81.24) * mm});
            skLineSegment(sketch, "E63.MirrorCS", {"start": v(-1752.67, 121.34) * mm, "end": v(-1752.67, 81.24) * mm});
            skArc(sketch, "E64.MirrorCS", {"start": v(-1355.67, 125.35) * mm, "mid": v(-1352.84, 124.18) * mm, "end": v(-1351.66, 121.34) * mm});
            skArc(sketch, "E65.MirrorCS", {"start": v(-1451.91, 81.24) * mm, "mid": v(-1453.09, 78.4) * mm, "end": v(-1455.92, 77.23) * mm});
            skLineSegment(sketch, "E66.MirrorCS", {"start": v(-1796.78, 125.35) * mm, "end": v(-1756.68, 125.35) * mm});
            skLineSegment(sketch, "E67.MirrorCS", {"start": v(-1650.41, 121.34) * mm, "end": v(-1650.41, 81.24) * mm});
            skLineSegment(sketch, "E68.MirrorCS", {"start": v(-1449.9, 121.34) * mm, "end": v(-1449.9, 81.24) * mm});
            skLineSegment(sketch, "E69.MirrorCS", {"start": v(-1796.78, 426.1) * mm, "end": v(-1756.68, 426.1) * mm});
            skLineSegment(sketch, "E70.MirrorCS", {"start": v(-1796.78, 225.6) * mm, "end": v(-1756.68, 225.6) * mm});
            skLineSegment(sketch, "E71.MirrorCS", {"start": v(-1445.9, 125.35) * mm, "end": v(-1405.8, 125.35) * mm});
            skLineSegment(sketch, "E72.MirrorCS", {"start": v(-1546.15, 125.35) * mm, "end": v(-1506.05, 125.35) * mm});
            skLineSegment(sketch, "E73.MirrorCS", {"start": v(-1646.4, 125.35) * mm, "end": v(-1606.3, 125.35) * mm});
            skArc(sketch, "E74.MirrorCS", {"start": v(-1756.68, 526.35) * mm, "mid": v(-1753.84, 525.18) * mm, "end": v(-1752.67, 522.34) * mm});
            skArc(sketch, "E75.MirrorCS", {"start": v(-1756.68, 225.6) * mm, "mid": v(-1753.84, 224.43) * mm, "end": v(-1752.67, 221.6) * mm});
            skLineSegment(sketch, "E76.MirrorCS", {"start": v(-1301.54, 121.34) * mm, "end": v(-1301.54, 81.24) * mm});
            skLineSegment(sketch, "E77.MirrorCS", {"start": v(-1401.79, 121.34) * mm, "end": v(-1401.79, 81.24) * mm});
            skLineSegment(sketch, "E78.MirrorCS", {"start": v(-1602.29, 121.34) * mm, "end": v(-1602.29, 81.24) * mm});
            skArc(sketch, "E79.MirrorCS", {"start": v(-1800.79, 221.6) * mm, "mid": v(-1799.61, 224.43) * mm, "end": v(-1796.78, 225.6) * mm});
            skLineSegment(sketch, "E80.MirrorCS", {"start": v(-1800.79, 221.6) * mm, "end": v(-1800.79, 181.5) * mm});
            skArc(sketch, "E81.MirrorCS", {"start": v(-1301.54, 81.24) * mm, "mid": v(-1302.71, 78.4) * mm, "end": v(-1305.55, 77.23) * mm});
            skArc(sketch, "E82.MirrorCS", {"start": v(-1796.78, 377.98) * mm, "mid": v(-1799.61, 379.16) * mm, "end": v(-1800.79, 382) * mm});
            skArc(sketch, "E83.MirrorCS", {"start": v(-1646.4, 77.23) * mm, "mid": v(-1649.24, 78.4) * mm, "end": v(-1650.41, 81.24) * mm});
            skArc(sketch, "E84.MirrorCS", {"start": v(-1746.65, 77.23) * mm, "mid": v(-1749.49, 78.4) * mm, "end": v(-1750.66, 81.24) * mm});
            skArc(sketch, "E85.MirrorCS", {"start": v(-1345.65, 77.23) * mm, "mid": v(-1348.48, 78.4) * mm, "end": v(-1349.66, 81.24) * mm});
            skArc(sketch, "E86.MirrorCS", {"start": v(-1445.9, 77.23) * mm, "mid": v(-1448.73, 78.4) * mm, "end": v(-1449.9, 81.24) * mm});
            skArc(sketch, "E87.MirrorCS", {"start": v(-1546.15, 77.23) * mm, "mid": v(-1548.98, 78.4) * mm, "end": v(-1550.16, 81.24) * mm});
            skLineSegment(sketch, "E88.MirrorCS", {"start": v(-1600.28, 121.34) * mm, "end": v(-1600.28, 81.24) * mm});
            skLineSegment(sketch, "E89.MirrorCS", {"start": v(-1700.54, 121.34) * mm, "end": v(-1700.54, 81.24) * mm});
            skLineSegment(sketch, "E90.MirrorCS", {"start": v(-1399.78, 121.34) * mm, "end": v(-1399.78, 81.24) * mm});
            skLineSegment(sketch, "E91.MirrorCS", {"start": v(-1500.03, 121.34) * mm, "end": v(-1500.03, 81.24) * mm});
            skLineSegment(sketch, "E92.MirrorCS", {"start": v(-1752.67, 522.34) * mm, "end": v(-1752.67, 482.24) * mm});
            skLineSegment(sketch, "E93.MirrorCS", {"start": v(-1752.67, 422.1) * mm, "end": v(-1752.67, 382) * mm});
            skArc(sketch, "E94.MirrorCS", {"start": v(-1600.28, 121.34) * mm, "mid": v(-1599.11, 124.18) * mm, "end": v(-1596.27, 125.35) * mm});
            skArc(sketch, "E95.MirrorCS", {"start": v(-1700.54, 121.34) * mm, "mid": v(-1699.36, 124.18) * mm, "end": v(-1696.53, 125.35) * mm});
            skArc(sketch, "E96.MirrorCS", {"start": v(-1399.78, 121.34) * mm, "mid": v(-1398.6, 124.18) * mm, "end": v(-1395.77, 125.35) * mm});
            skArc(sketch, "E97.MirrorCS", {"start": v(-1500.03, 121.34) * mm, "mid": v(-1498.86, 124.18) * mm, "end": v(-1496.02, 125.35) * mm});
            skLineSegment(sketch, "E98.MirrorCS", {"start": v(-1596.27, 125.35) * mm, "end": v(-1556.17, 125.35) * mm});
            skLineSegment(sketch, "E99.MirrorCS", {"start": v(-1696.53, 125.35) * mm, "end": v(-1656.43, 125.35) * mm});
            skLineSegment(sketch, "E100.MirrorCS", {"start": v(-1800.79, 121.34) * mm, "end": v(-1800.79, 81.24) * mm});
            skLineSegment(sketch, "E101.MirrorCS", {"start": v(-1395.77, 125.35) * mm, "end": v(-1355.67, 125.35) * mm});
            skLineSegment(sketch, "E102.MirrorCS", {"start": v(-1496.02, 125.35) * mm, "end": v(-1455.92, 125.35) * mm});
            skLineSegment(sketch, "E103.MirrorCS", {"start": v(-1451.91, 121.34) * mm, "end": v(-1451.91, 81.24) * mm});
            skLineSegment(sketch, "E104.MirrorCS", {"start": v(-1552.16, 121.34) * mm, "end": v(-1552.16, 81.24) * mm});
            skLineSegment(sketch, "E105.MirrorCS", {"start": v(-1652.42, 121.34) * mm, "end": v(-1652.42, 81.24) * mm});
            skLineSegment(sketch, "E106.MirrorCS", {"start": v(-1800.79, 371.97) * mm, "end": v(-1800.79, 331.87) * mm});
            skArc(sketch, "E107.MirrorCS", {"start": v(-1556.17, 125.35) * mm, "mid": v(-1553.34, 124.18) * mm, "end": v(-1552.16, 121.34) * mm});
            skArc(sketch, "E108.MirrorCS", {"start": v(-1656.43, 125.35) * mm, "mid": v(-1653.59, 124.18) * mm, "end": v(-1652.42, 121.34) * mm});
            skLineSegment(sketch, "E109.MirrorCS", {"start": v(-1800.79, 171.47) * mm, "end": v(-1800.79, 131.36) * mm});
            skArc(sketch, "E110.MirrorCS", {"start": v(-1455.92, 125.35) * mm, "mid": v(-1453.09, 124.18) * mm, "end": v(-1451.91, 121.34) * mm});
            skArc(sketch, "E111.MirrorCS", {"start": v(-1552.16, 81.24) * mm, "mid": v(-1553.34, 78.4) * mm, "end": v(-1556.17, 77.23) * mm});
            skArc(sketch, "E112.MirrorCS", {"start": v(-1652.42, 81.24) * mm, "mid": v(-1653.59, 78.4) * mm, "end": v(-1656.43, 77.23) * mm});
            skArc(sketch, "E113.MirrorCS", {"start": v(-1800.79, 121.34) * mm, "mid": v(-1799.61, 124.18) * mm, "end": v(-1796.78, 125.35) * mm});
            skArc(sketch, "E114.MirrorCS", {"start": v(-1351.66, 81.24) * mm, "mid": v(-1352.84, 78.4) * mm, "end": v(-1355.67, 77.23) * mm});
            skArc(sketch, "E115.MirrorCS", {"start": v(-1796.78, 327.86) * mm, "mid": v(-1799.61, 329.03) * mm, "end": v(-1800.79, 331.87) * mm});
            skArc(sketch, "E116.MirrorCS", {"start": v(-1752.67, 81.24) * mm, "mid": v(-1753.84, 78.4) * mm, "end": v(-1756.68, 77.23) * mm});
            skLineSegment(sketch, "E117.MirrorCS", {"start": v(-1796.78, 127.35) * mm, "end": v(-1756.68, 127.35) * mm});
            skLineSegment(sketch, "E118.MirrorCS", {"start": v(-1496.02, 77.23) * mm, "end": v(-1455.92, 77.23) * mm});
            skArc(sketch, "E119.MirrorCS", {"start": v(-1496.02, 77.23) * mm, "mid": v(-1498.86, 78.4) * mm, "end": v(-1500.03, 81.24) * mm});
            skLineSegment(sketch, "E120.MirrorCS", {"start": v(-1752.67, 271.72) * mm, "end": v(-1752.67, 231.62) * mm});
            skLineSegment(sketch, "E121.MirrorCS", {"start": v(-1796.78, 526.35) * mm, "end": v(-1756.68, 526.35) * mm});
            skLineSegment(sketch, "E122.MirrorCS", {"start": v(-1796.78, 325.85) * mm, "end": v(-1756.68, 325.85) * mm});
            skArc(sketch, "E123.MirrorCS", {"start": v(-1401.79, 81.24) * mm, "mid": v(-1402.96, 78.4) * mm, "end": v(-1405.8, 77.23) * mm});
            skArc(sketch, "E124.MirrorCS", {"start": v(-1752.67, 281.74) * mm, "mid": v(-1753.84, 278.9) * mm, "end": v(-1756.68, 277.73) * mm});
            skLineSegment(sketch, "E125.MirrorCS", {"start": v(-1746.65, 77.23) * mm, "end": v(-1706.55, 77.23) * mm});
            skLineSegment(sketch, "E126.MirrorCS", {"start": v(-1345.65, 77.23) * mm, "end": v(-1305.55, 77.23) * mm});
            skLineSegment(sketch, "E127.MirrorCS", {"start": v(-1546.15, 77.23) * mm, "end": v(-1506.05, 77.23) * mm});
            skLineSegment(sketch, "E128.MirrorCS", {"start": v(-1646.4, 77.23) * mm, "end": v(-1606.3, 77.23) * mm});
            skLineSegment(sketch, "E129.MirrorCS", {"start": v(-1796.78, 377.98) * mm, "end": v(-1756.68, 377.98) * mm});
            skLineSegment(sketch, "E130.MirrorCS", {"start": v(-1796.78, 277.73) * mm, "end": v(-1756.68, 277.73) * mm});
            skLineSegment(sketch, "E131.MirrorCS", {"start": v(-1752.67, 221.6) * mm, "end": v(-1752.67, 181.5) * mm});
            skLineSegment(sketch, "E132.MirrorCS", {"start": v(-1800.79, 81.24) * mm, "end": v(-1750.66, 81.24) * mm, "construction": true});
            skLineSegment(sketch, "E133.MirrorCS", {"start": v(-1796.78, 375.98) * mm, "end": v(-1756.68, 375.98) * mm});
            skArc(sketch, "E134.MirrorCS", {"start": v(-1800.79, 271.72) * mm, "mid": v(-1799.61, 274.55) * mm, "end": v(-1796.78, 275.73) * mm});
            skArc(sketch, "E135.MirrorCS", {"start": v(-1800.79, 371.97) * mm, "mid": v(-1799.61, 374.8) * mm, "end": v(-1796.78, 375.98) * mm});
            skArc(sketch, "E136.MirrorCS", {"start": v(-1796.78, 227.6) * mm, "mid": v(-1799.61, 228.78) * mm, "end": v(-1800.79, 231.62) * mm});
            skArc(sketch, "E137.MirrorCS", {"start": v(-1796.78, 428.1) * mm, "mid": v(-1799.61, 429.28) * mm, "end": v(-1800.79, 432.12) * mm});
            skLineSegment(sketch, "E138.MirrorCS", {"start": v(-1796.78, 77.23) * mm, "end": v(-1756.68, 77.23) * mm});
            skLineSegment(sketch, "E139.MirrorCS", {"start": v(-1596.27, 77.23) * mm, "end": v(-1556.17, 77.23) * mm});
            skLineSegment(sketch, "E140.MirrorCS", {"start": v(-1696.53, 77.23) * mm, "end": v(-1656.43, 77.23) * mm});
            skLineSegment(sketch, "E141.MirrorCS", {"start": v(-1796.78, 227.6) * mm, "end": v(-1756.68, 227.6) * mm});
            skLineSegment(sketch, "E142.MirrorCS", {"start": v(-1395.77, 77.23) * mm, "end": v(-1355.67, 77.23) * mm});
            skArc(sketch, "E143.MirrorCS", {"start": v(-1596.27, 77.23) * mm, "mid": v(-1599.11, 78.4) * mm, "end": v(-1600.28, 81.24) * mm});
            skArc(sketch, "E144.MirrorCS", {"start": v(-1696.53, 77.23) * mm, "mid": v(-1699.36, 78.4) * mm, "end": v(-1700.54, 81.24) * mm});
            skArc(sketch, "E145.MirrorCS", {"start": v(-1796.78, 77.23) * mm, "mid": v(-1799.61, 78.4) * mm, "end": v(-1800.79, 81.24) * mm});
            skArc(sketch, "E146.MirrorCS", {"start": v(-1752.67, 231.62) * mm, "mid": v(-1753.84, 228.78) * mm, "end": v(-1756.68, 227.6) * mm});
            skArc(sketch, "E147.MirrorCS", {"start": v(-1752.67, 532.37) * mm, "mid": v(-1753.84, 529.53) * mm, "end": v(-1756.68, 528.36) * mm});
            skArc(sketch, "E148.MirrorCS", {"start": v(-1752.67, 331.87) * mm, "mid": v(-1753.84, 329.03) * mm, "end": v(-1756.68, 327.86) * mm});
            skLineSegment(sketch, "E149.MirrorCS", {"start": v(-1752.67, 572.47) * mm, "end": v(-1752.67, 532.37) * mm});
            skLineSegment(sketch, "E150.MirrorCS", {"start": v(-1752.67, 371.97) * mm, "end": v(-1752.67, 331.87) * mm});
            skArc(sketch, "E151.MirrorCS", {"start": v(-1756.68, 325.85) * mm, "mid": v(-1753.84, 324.68) * mm, "end": v(-1752.67, 321.84) * mm});
            skArc(sketch, "E152.MirrorCS", {"start": v(-1800.79, 522.34) * mm, "mid": v(-1799.61, 525.18) * mm, "end": v(-1796.78, 526.35) * mm});
            skArc(sketch, "E153.MirrorCS", {"start": v(-1800.79, 422.1) * mm, "mid": v(-1799.61, 424.93) * mm, "end": v(-1796.78, 426.1) * mm});
            skLineSegment(sketch, "E154.MirrorCS", {"start": v(-1800.79, 522.34) * mm, "end": v(-1800.79, 482.24) * mm});
            skLineSegment(sketch, "E155.MirrorCS", {"start": v(-1800.79, 422.1) * mm, "end": v(-1800.79, 382) * mm});
            skLineSegment(sketch, "E156.MirrorCS", {"start": v(-1800.79, 321.84) * mm, "end": v(-1800.79, 281.74) * mm});
            skArc(sketch, "E157.MirrorCS", {"start": v(-1796.78, 277.73) * mm, "mid": v(-1799.61, 278.9) * mm, "end": v(-1800.79, 281.74) * mm});
            skLineSegment(sketch, "E158.MirrorCS", {"start": v(-1445.9, 77.23) * mm, "end": v(-1405.8, 77.23) * mm});
            skLineSegment(sketch, "E159.MirrorCS", {"start": v(-1752.67, 321.84) * mm, "end": v(-1752.67, 281.74) * mm});
            skLineSegment(sketch, "E160.MirrorCS", {"start": v(-1796.78, 275.73) * mm, "end": v(-1756.68, 275.73) * mm});
            skArc(sketch, "E161.MirrorCS", {"start": v(-1756.68, 275.73) * mm, "mid": v(-1753.84, 274.55) * mm, "end": v(-1752.67, 271.72) * mm});
            skArc(sketch, "E162.MirrorCS", {"start": v(-1756.68, 375.98) * mm, "mid": v(-1753.84, 374.8) * mm, "end": v(-1752.67, 371.97) * mm});
            skLineSegment(sketch, "E163.MirrorCS", {"start": v(-1800.79, 472.22) * mm, "end": v(-1800.79, 432.12) * mm});
            skLineSegment(sketch, "E164.MirrorCS", {"start": v(-1800.79, 271.72) * mm, "end": v(-1800.79, 231.62) * mm});
            skLineSegment(sketch, "E165.MirrorCS", {"start": v(-1796.78, 428.1) * mm, "end": v(-1756.68, 428.1) * mm});
            skLineSegment(sketch, "E166.MirrorCS", {"start": v(-1796.78, 327.86) * mm, "end": v(-1756.68, 327.86) * mm});
            skArc(sketch, "E167.MirrorCS", {"start": v(-1395.77, 77.23) * mm, "mid": v(-1398.6, 78.4) * mm, "end": v(-1399.78, 81.24) * mm});
            skLineSegment(sketch, "E168.MirrorCS", {"start": v(-1796.78, 576.48) * mm, "end": v(-1756.68, 576.48) * mm});
            skArc(sketch, "E169.MirrorCS", {"start": v(-1756.68, 576.48) * mm, "mid": v(-1753.84, 575.3) * mm, "end": v(-1752.67, 572.47) * mm});
            skArc(sketch, "E170.MirrorCS", {"start": v(-1800.79, 572.47) * mm, "mid": v(-1799.61, 575.3) * mm, "end": v(-1796.78, 576.48) * mm});
            skArc(sketch, "E171.MirrorCS", {"start": v(-1796.78, 528.36) * mm, "mid": v(-1799.61, 529.53) * mm, "end": v(-1800.79, 532.37) * mm});
            skLineSegment(sketch, "E172.MirrorCS", {"start": v(-1796.78, 528.36) * mm, "end": v(-1756.68, 528.36) * mm});
            skLineSegment(sketch, "E173.MirrorCS", {"start": v(-1345.65, 125.35) * mm, "end": v(-1305.55, 125.35) * mm});
            skLineSegment(sketch, "E174.MirrorCS", {"start": v(-1800.79, 572.47) * mm, "end": v(-1800.79, 532.37) * mm});
            skArc(sketch, "E175.MirrorCS", {"start": v(-1305.55, 125.35) * mm, "mid": v(-1302.71, 124.18) * mm, "end": v(-1301.54, 121.34) * mm});
            skPoint(sketch, "E176.MirrorP", {"position": v(-1752.67, 125.35) * mm});
            skPoint(sketch, "E177.MirrorP", {"position": v(-1750.66, 125.35) * mm});
            skPoint(sketch, "E178.MirrorP", {"position": v(-1550.16, 125.35) * mm});
            skPoint(sketch, "E179.MirrorP", {"position": v(-1700.54, 125.35) * mm});
            skPoint(sketch, "E180.MirrorP", {"position": v(-1349.66, 125.35) * mm});
            skPoint(sketch, "E181.MirrorP", {"position": v(-1500.03, 125.35) * mm});
            skPoint(sketch, "E182.MirrorP", {"position": v(-1650.41, 125.35) * mm});
            skPoint(sketch, "E183.MirrorP", {"position": v(-1800.79, 125.35) * mm});
            skPoint(sketch, "E184.MirrorP", {"position": v(-1752.67, 77.23) * mm});
            skPoint(sketch, "E185.MirrorP", {"position": v(-1449.9, 125.35) * mm});
            skPoint(sketch, "E186.MirrorP", {"position": v(-1600.28, 125.35) * mm});
            skLineSegment(sketch, "E187.MirrorCS", {"start": v(-1801.62, -451.01) * mm, "end": v(-1801.62, 0.12) * mm});
            skLineSegment(sketch, "E188.MirrorCS", {"start": v(-1801.62, 0.12) * mm, "end": v(-1300.37, 0.12) * mm});
            skLineSegment(sketch, "E189.MirrorCS", {"start": v(-1300.37, 0.12) * mm, "end": v(-1801.62, -451.01) * mm});
            skLineSegment(sketch, "E190.MirrorCS", {"start": v(-1414.56, 0.12) * mm, "end": v(-1801.62, -348.24) * mm});
            skPoint(sketch, "E191.MirrorP", {"position": v(-1399.78, 125.35) * mm});
            skPoint(sketch, "E192.MirrorP", {"position": v(-1801.62, 651.75) * mm});
            skPoint(sketch, "E193.MirrorP", {"position": v(-1300.37, 76.5) * mm});
            skLineSegment(sketch, "E194", {"start": v(-1805.62, 651.75) * mm, "end": v(-2201.62, 651.75) * mm});
            skLineSegment(sketch, "E195", {"start": v(-1801.62, 647.75) * mm, "end": v(-1801.62, 76.5) * mm});
            skLineSegment(sketch, "E196", {"start": v(-1801.62, 76.5) * mm, "end": v(-1300.37, 76.5) * mm});
            skLineSegment(sketch, "E197", {"start": v(-1300.37, 0.12) * mm, "end": v(-1300.37, 76.5) * mm});
            skLineSegment(sketch, "E198", {"start": v(-2201.62, 651.75) * mm, "end": v(-2201.62, -451.01) * mm});
            skLineSegment(sketch, "E199", {"start": v(-2201.62, -451.01) * mm, "end": v(-1801.62, -451.01) * mm});
            skArc(sketch, "E200.filletArc", {"start": v(-1801.62, 647.75) * mm, "mid": v(-1802.8, 650.57) * mm, "end": v(-1805.62, 651.75) * mm});
            skSolve(sketch);
        }
        {
            var Q0;
            Q0 = qSketchRegion(id + "F5", true);
            extrude(context, id + "F6", {"entities" : qUnion([Q0]), "operationType" : NewBodyOperationType.ADD, "oppositeDirection" : true, "depth" : 2100 * mm, "offsetDistance" : 25 * mm});
        }
    });
